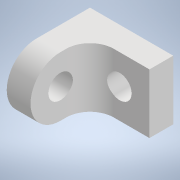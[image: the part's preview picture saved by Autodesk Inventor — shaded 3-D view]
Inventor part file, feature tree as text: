
AUTODESK INVENTOR PART (.ipt)
format: ipt  version: 2020 (Build 240168000, 168)  size: 143,872 bytes
history: native  units: mm
features: other x5, sketch x4, extrude x3
ambient origin geometry x8: Origin, YZ Plane, XZ Plane, XY Plane, X Axis, Y Axis, Z Axis, Center Point
bodies: Body1 (feature_tree)
feature tree (12):
  other  "Sólido1"
  extrude  "Extrusão1"  Depth=5.0mm TaperAngle=0.0deg
  extrude  "Extrusão2"  Depth=2.5mm
  extrude  "Extrusão3"  Depth=2.5mm TaperAngle=0.0deg
  sketch  "Esboço4"  dims[d8=2.5mm d9=2.5mm d10=4.25mm d11=0.0mm]
  sketch  "Esboço1"  dims[d0=2.0mm d1=5.0mm d2=0.0mm]
  sketch  "Esboço2"  dims[d3=2.0mm d4=2.5mm]
  sketch  "Esboço3"  dims[d5=2.5mm d6=4.25mm d7=0.0mm]
  other  "Referência1"
  other  "<userpath>\Desktop\rabo\3d\ela.iam"
  other  "ela.iam"
  other  "PCB:1"
